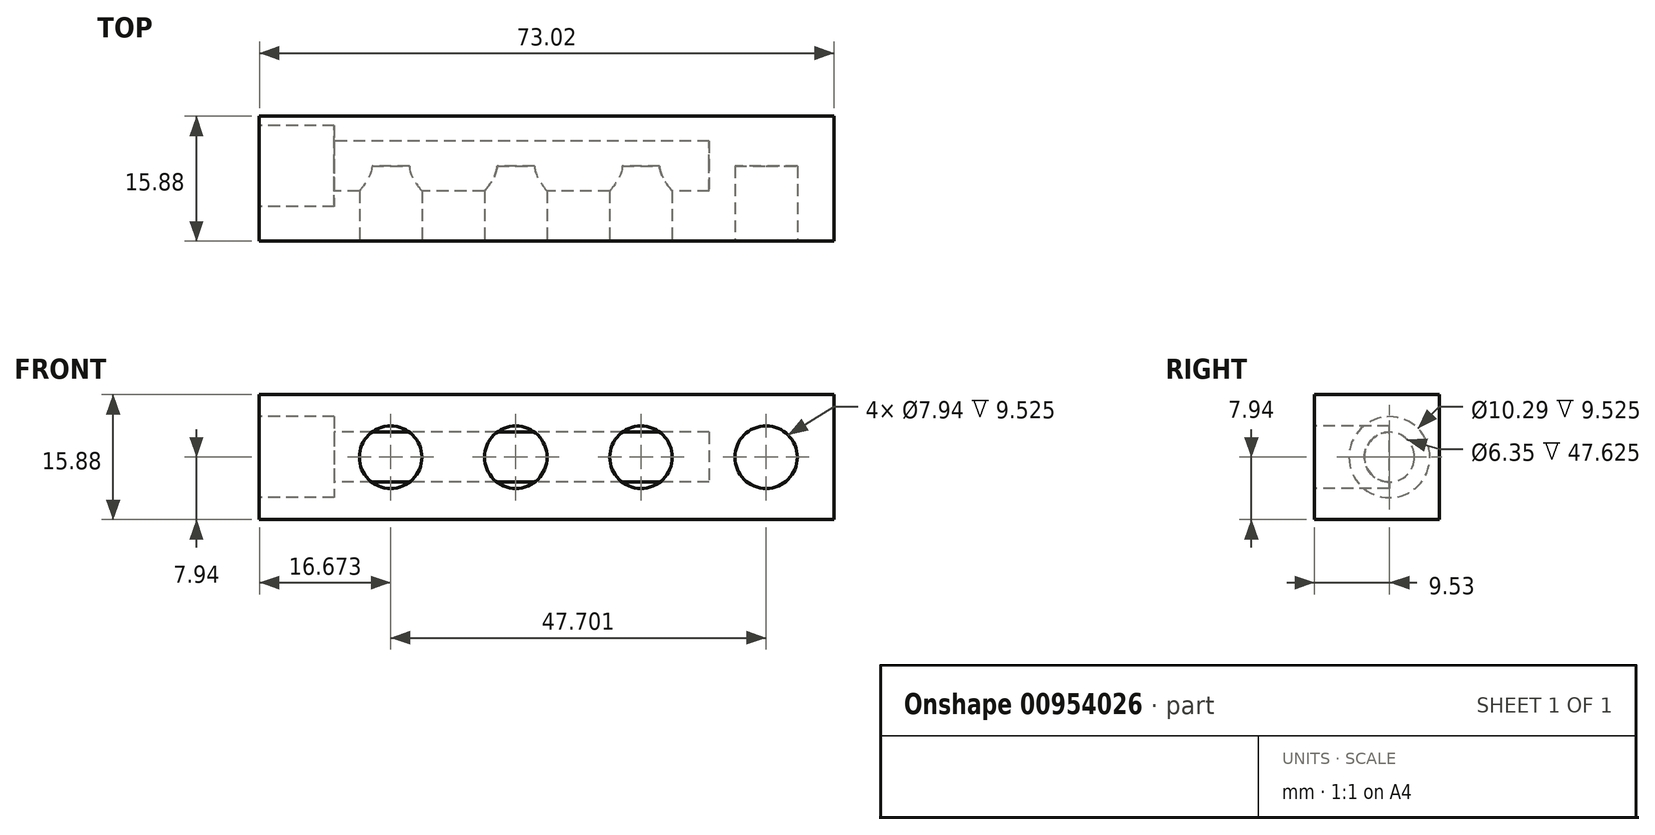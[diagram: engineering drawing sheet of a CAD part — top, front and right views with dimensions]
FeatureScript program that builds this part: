
annotation { "Feature Type Name" : "Feature", "Feature Type Description" : "" }
export const myFeature = defineFeature(function(context is Context, id is Id, definition is map)
    precondition{}
    {
        {
            var Q0;
            Q0=qCreatedBy(makeId("Front.planeOp"),FACE);
            var sketch = newSketch(context, id + "F0", { "sketchPlane" : qUnion([Q0])});
            skLineSegment(sketch, "E0.bottom", {"start": v(36.51, 5.13) * mm, "end": v(-36.51, 5.13) * mm, "construction": true});
            skLineSegment(sketch, "E0.top", {"start": v(36.51, -5.13) * mm, "end": v(-36.51, -5.13) * mm, "construction": true});
            skLineSegment(sketch, "E0.left", {"start": v(36.51, 5.13) * mm, "end": v(36.51, -5.13) * mm, "construction": true});
            skLineSegment(sketch, "E0.right", {"start": v(-36.51, 5.13) * mm, "end": v(-36.51, -5.13) * mm, "construction": true});
            skPoint(sketch, "E0.middle", {"position": v(0, 0) * mm});
            skLineSegment(sketch, "E1.bottom", {"start": v(-36.51, 7.94) * mm, "end": v(36.51, 7.94) * mm});
            skLineSegment(sketch, "E1.top", {"start": v(-36.51, -7.94) * mm, "end": v(36.51, -7.94) * mm});
            skLineSegment(sketch, "E1.left", {"start": v(-36.51, 7.94) * mm, "end": v(-36.51, -7.94) * mm});
            skLineSegment(sketch, "E1.right", {"start": v(36.51, 7.94) * mm, "end": v(36.51, -7.94) * mm});
            skSolve(sketch);
        }
        {
            var Q0;
            Q0 = qSketchRegion(id + "F0", true);
            extrude(context, id + "F1", {"entities" : qUnion([Q0]), "depth" : 9.52 * mm, "offsetDistance" : 25.4 * mm, "hasSecondDirection" : true, "secondDirectionOppositeDirection" : true, "secondDirectionDepth" : 6.35 * mm});
        }
        {
            var Q0;
            Q0=makeQuery(id+"F1.opExtrude","SWEPT_FACE",FACE,{"disambiguationData":[OSD([sQuery(id+"F0.wireOp",EDGE,"E1.left")])]});
            var sketch = newSketch(context, id + "F2", { "sketchPlane" : qUnion([Q0])});
            skCircle(sketch, "E2", {"center": v(0, 0) * mm, "radius": 5.14 * mm});
            skSolve(sketch);
        }
        {
            var Q0;
            Q0 = qSketchRegion(id + "F2", true);
            extrude(context, id + "F3", {"entities" : qUnion([Q0]), "operationType" : NewBodyOperationType.REMOVE, "oppositeDirection" : true, "depth" : 9.52 * mm, "offsetDistance" : 25.4 * mm});
        }
        {
            var Q0;
            Q0=makeQuery(id+"F1.opExtrude","SWEPT_FACE",FACE,{"disambiguationData":[OSD([sQuery(id+"F0.wireOp",EDGE,"E1.left")])]});
            var sketch = newSketch(context, id + "F4", { "sketchPlane" : qUnion([Q0])});
            skCircle(sketch, "E3", {"center": v(0, 0) * mm, "radius": 3.18 * mm});
            skSolve(sketch);
        }
        {
            var Q0;
            Q0 = qSketchRegion(id + "F4", true);
            extrude(context, id + "F5", {"entities" : qUnion([Q0]), "operationType" : NewBodyOperationType.REMOVE, "oppositeDirection" : true, "depth" : 57.15 * mm, "offsetDistance" : 25.4 * mm});
        }
        {
            var Q0;
            Q0=makeQuery(id+"F1.opExtrude","CAP_FACE",FACE,{"disambiguationData":[OSD([sQuery(id+"F0.wireOp",EDGE,"E1.bottom"),sQuery(id+"F0.wireOp",EDGE,"E1.top"),sQuery(id+"F0.wireOp",EDGE,"E1.left"),sQuery(id+"F0.wireOp",EDGE,"E1.right")])],"isStart":false});
            var sketch = newSketch(context, id + "F6", { "sketchPlane" : qUnion([Q0])});
            skCircle(sketch, "E4", {"center": v(-3.94, 0) * mm, "radius": 3.97 * mm});
            skCircle(sketch, "E5", {"center": v(-19.84, 0) * mm, "radius": 3.97 * mm});
            skCircle(sketch, "E6", {"center": v(11.96, 0) * mm, "radius": 3.97 * mm});
            skCircle(sketch, "E7", {"center": v(27.86, 0) * mm, "radius": 3.97 * mm});
            skSolve(sketch);
        }
        {
            var Q0;
            Q0 = qSketchRegion(id + "F6", true);
            var Q1;
            Q1=qCreatedBy(makeId("Front.planeOp"),FACE);
            extrude(context, id + "F7", {"entities" : qUnion([Q0]), "operationType" : NewBodyOperationType.REMOVE, "endBound" : BoundingType.UP_TO_SURFACE, "oppositeDirection" : true, "depth" : 25.4 * mm, "endBoundEntityFace" : qUnion([Q1]), "offsetDistance" : 25.4 * mm});
        }
    });
